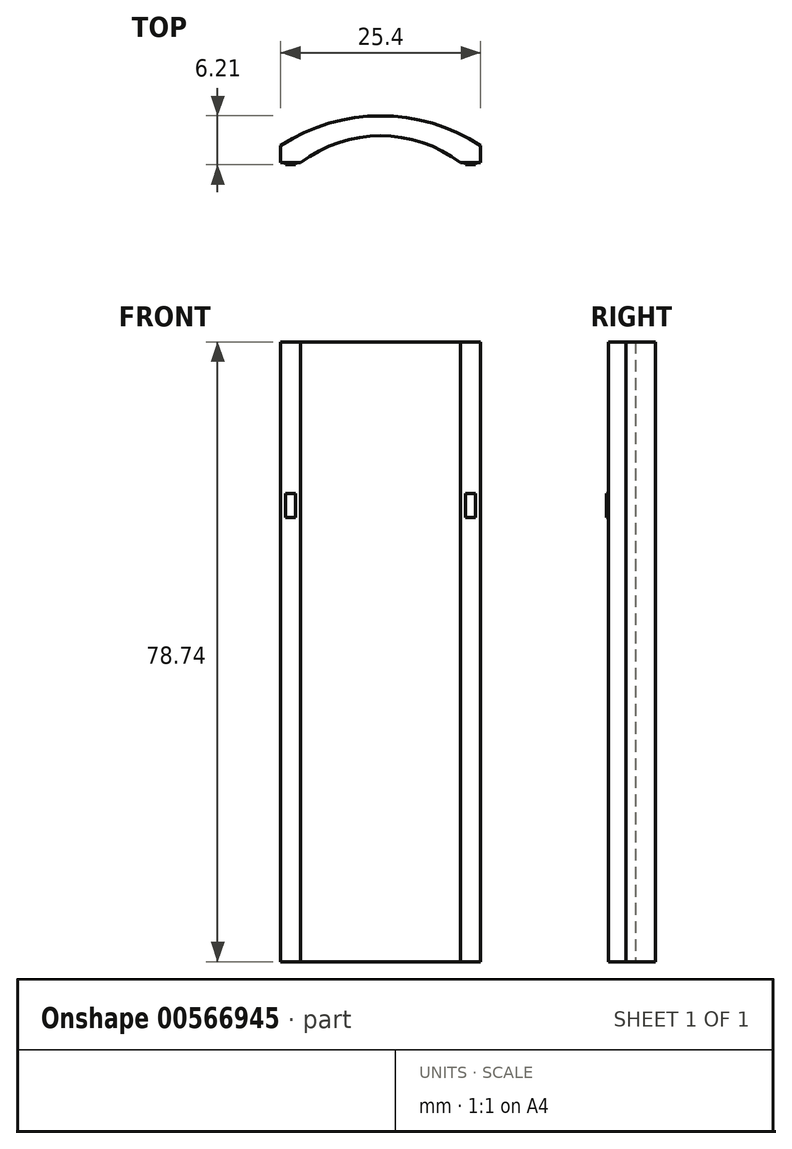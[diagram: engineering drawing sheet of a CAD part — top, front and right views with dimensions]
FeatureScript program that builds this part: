
annotation { "Feature Type Name" : "Feature", "Feature Type Description" : "" }
export const myFeature = defineFeature(function(context is Context, id is Id, definition is map)
    precondition{}
    {
        {
            var Q0;
            Q0=qCreatedBy(makeId("Top.planeOp"),FACE);
            var sketch = newSketch(context, id + "F0", { "sketchPlane" : qUnion([Q0])});
            skArc(sketch, "E0", {"start": v(12.7, -493.8) * mm, "mid": v(0, -490.05) * mm, "end": v(-12.7, -493.8) * mm});
            skPoint(sketch, "E1.visualSharp", {"position": v(-12.7, -493.8) * mm});
            skLineSegment(sketch, "E2", {"start": v(-12.7, -493.8) * mm, "end": v(-12.7, -496) * mm});
            skLineSegment(sketch, "E3", {"start": v(-12.7, -496) * mm, "end": v(-10.16, -496) * mm});
            skLineSegment(sketch, "E4", {"start": v(12.7, -493.8) * mm, "end": v(12.7, -496) * mm});
            skLineSegment(sketch, "E5", {"start": v(12.7, -496) * mm, "end": v(10.16, -496) * mm});
            skArc(sketch, "E6", {"start": v(10.16, -496) * mm, "mid": v(0, -492.6) * mm, "end": v(-10.16, -496) * mm});
            skLineSegment(sketch, "E7", {"start": v(0, -490.05) * mm, "end": v(0, -492.6) * mm, "construction": true});
            skLineSegment(sketch, "E8", {"start": v(-10.16, -496) * mm, "end": v(10.16, -496) * mm, "construction": true});
            skSolve(sketch);
        }
        {
            var Q0;
            Q0 = qSketchRegion(id + "F0", true);
            extrude(context, id + "F1", {"entities" : qUnion([Q0]), "depth" : 78.74 * mm, "offsetDistance" : 25.4 * mm});
        }
        {
            var Q0;
            Q0=makeQuery(id+"F1.opExtrude","SWEPT_FACE",FACE,{"disambiguationData":[OSD([sQuery(id+"F0.wireOp",EDGE,"E5")])]});
            var sketch = newSketch(context, id + "F2", { "sketchPlane" : qUnion([Q0])});
            skLineSegment(sketch, "E9", {"start": v(10.8, 59.49) * mm, "end": v(12.7, 59.49) * mm});
            skLineSegment(sketch, "E10", {"start": v(5.74, 39.37) * mm, "end": v(5.95, 39.37) * mm, "construction": true});
            skLineSegment(sketch, "E11", {"start": v(10.8, 59.49) * mm, "end": v(10.8, 56.44) * mm});
            skLineSegment(sketch, "E12", {"start": v(10.8, 56.44) * mm, "end": v(12.06, 56.44) * mm});
            skLineSegment(sketch, "E13", {"start": v(12.06, 56.44) * mm, "end": v(12.06, 59.49) * mm});
            skLineSegment(sketch, "E14", {"start": v(10.8, 59.49) * mm, "end": v(10.16, 59.49) * mm, "construction": true});
            skSolve(sketch);
        }
        {
            var Q0;
            Q0=makeQuery(id+"F1.opExtrude","SWEPT_FACE",FACE,{"disambiguationData":[OSD([sQuery(id+"F0.wireOp",EDGE,"E3")])]});
            var sketch = newSketch(context, id + "F3", { "sketchPlane" : qUnion([Q0])});
            skLineSegment(sketch, "E15", {"start": v(-58.64, 285.92) * mm, "end": v(-55.69, 285.92) * mm, "construction": true});
            skLineSegment(sketch, "E16", {"start": v(-58.43, 285.92) * mm, "end": v(-55.9, 285.92) * mm});
            skLineSegment(sketch, "E17", {"start": v(-55.9, 285.92) * mm, "end": v(-55.69, 285.92) * mm, "construction": true});
            skLineSegment(sketch, "E18", {"start": v(-58.43, 285.92) * mm, "end": v(-58.64, 285.92) * mm, "construction": true});
            skLineSegment(sketch, "E19", {"start": v(-58.43, 285.92) * mm, "end": v(-58.43, 282.11) * mm});
            skLineSegment(sketch, "E20", {"start": v(-58.43, 282.11) * mm, "end": v(-55.9, 282.11) * mm});
            skLineSegment(sketch, "E21", {"start": v(-55.9, 282.11) * mm, "end": v(-55.9, 285.92) * mm});
            skLineSegment(sketch, "E22", {"start": v(-54.3, 267.01) * mm, "end": v(-51.36, 267.01) * mm, "construction": true});
            skLineSegment(sketch, "E23", {"start": v(-54.1, 267.01) * mm, "end": v(-51.56, 267.01) * mm});
            skLineSegment(sketch, "E24", {"start": v(-51.56, 267.01) * mm, "end": v(-51.36, 267.01) * mm, "construction": true});
            skLineSegment(sketch, "E25", {"start": v(-54.1, 267.01) * mm, "end": v(-54.3, 267.01) * mm, "construction": true});
            skLineSegment(sketch, "E26", {"start": v(-54.1, 267.01) * mm, "end": v(-54.1, 263.2) * mm});
            skLineSegment(sketch, "E27", {"start": v(-54.1, 263.2) * mm, "end": v(-51.56, 263.2) * mm});
            skLineSegment(sketch, "E28", {"start": v(-51.56, 263.2) * mm, "end": v(-51.56, 267.01) * mm});
            skLineSegment(sketch, "E29", {"start": v(-12.06, 59.49) * mm, "end": v(-10.8, 59.49) * mm});
            skLineSegment(sketch, "E30", {"start": v(-12.06, 59.49) * mm, "end": v(-12.06, 56.44) * mm});
            skLineSegment(sketch, "E31", {"start": v(-12.06, 56.44) * mm, "end": v(-10.8, 56.44) * mm});
            skLineSegment(sketch, "E32", {"start": v(-10.8, 56.44) * mm, "end": v(-10.8, 59.49) * mm});
            skLineSegment(sketch, "E33", {"start": v(-10.8, 59.49) * mm, "end": v(-10.16, 59.49) * mm, "construction": true});
            skSolve(sketch);
        }
        {
            var Q0;
            Q0 = qSketchRegion(id + "F3", true);
            var Q1;
            Q1 = qSketchRegion(id + "F2", true);
            extrude(context, id + "F4", {"entities" : qUnion([Q0, Q1]), "operationType" : NewBodyOperationType.ADD, "depth" : 0.25 * mm, "offsetDistance" : 25.4 * mm, "hasSecondDirection" : true, "secondDirectionOppositeDirection" : true, "secondDirectionDepth" : 0.25 * mm});
        }
        {
            var Q0;
            Q0=makeQuery(id+"F4.opExtrude","SWEPT_BODY",BODY,{"disambiguationData":[OSD([sQuery(id+"F3.wireOp",EDGE,"E16"),sQuery(id+"F3.wireOp",EDGE,"E19"),sQuery(id+"F3.wireOp",EDGE,"E20"),sQuery(id+"F3.wireOp",EDGE,"E21")])]});
            var Q1;
            Q1=makeQuery(id+"F4.opExtrude","SWEPT_BODY",BODY,{"disambiguationData":[OSD([sQuery(id+"F3.wireOp",EDGE,"E23"),sQuery(id+"F3.wireOp",EDGE,"E26"),sQuery(id+"F3.wireOp",EDGE,"E27"),sQuery(id+"F3.wireOp",EDGE,"E28")])]});
            deleteBodies(context, id + "F5", {"entities" : qUnion([Q0, Q1])});
        }
    });
